# Revit family: VTi.902.I_Пресс_фитинг_Внут резьба_Нерж_VALTEC
name_source: partatom
category: Соединительные детали трубопроводов
units: mm (PartAtom-declared; Revit-internal decimal feet)

## family parameters
Всегда вертикально = Да
На основе рабочей плоскости = Нет
Общий = Нет
При загрузке вырезать с полостями = Нет
Размер круглого соединителя = Использовать диаметр
Тип детали = Соединение

## types (12) — shared parameters
ADSK_Единица измерения = шт.
ADSK_Количество = 1
ADSK_Материал = Сталь, нержавеющая - VALTEC
zero-valued in all types: Отметка по умолчанию

## type names (no varying parameters)
- Пресс-фитинг из нержавеющей стали с внутренней резьбой 12 мм х 1/2"
- Пресс-фитинг из нержавеющей стали с внутренней резьбой 15 мм х 1/2"
- Пресс-фитинг из нержавеющей стали с внутренней резьбой 18 мм х 1/2"
- Пресс-фитинг из нержавеющей стали с внутренней резьбой 18 мм х 3/4"
- Пресс-фитинг из нержавеющей стали с внутренней резьбой 22 мм х 1/2"
- Пресс-фитинг из нержавеющей стали с внутренней резьбой 22 мм х 3/4"
- Пресс-фитинг из нержавеющей стали с внутренней резьбой 28 мм х 1"
- Пресс-фитинг из нержавеющей стали с внутренней резьбой 28 мм х 3/4"
- Пресс-фитинг из нержавеющей стали с внутренней резьбой 35 мм х 1"
- Пресс-фитинг из нержавеющей стали с внутренней резьбой 35 мм х 1 1/4"
- Пресс-фитинг из нержавеющей стали с внутренней резьбой 42 мм х 1 1/2"
- Пресс-фитинг из нержавеющей стали с внутренней резьбой 54мм х 2"
